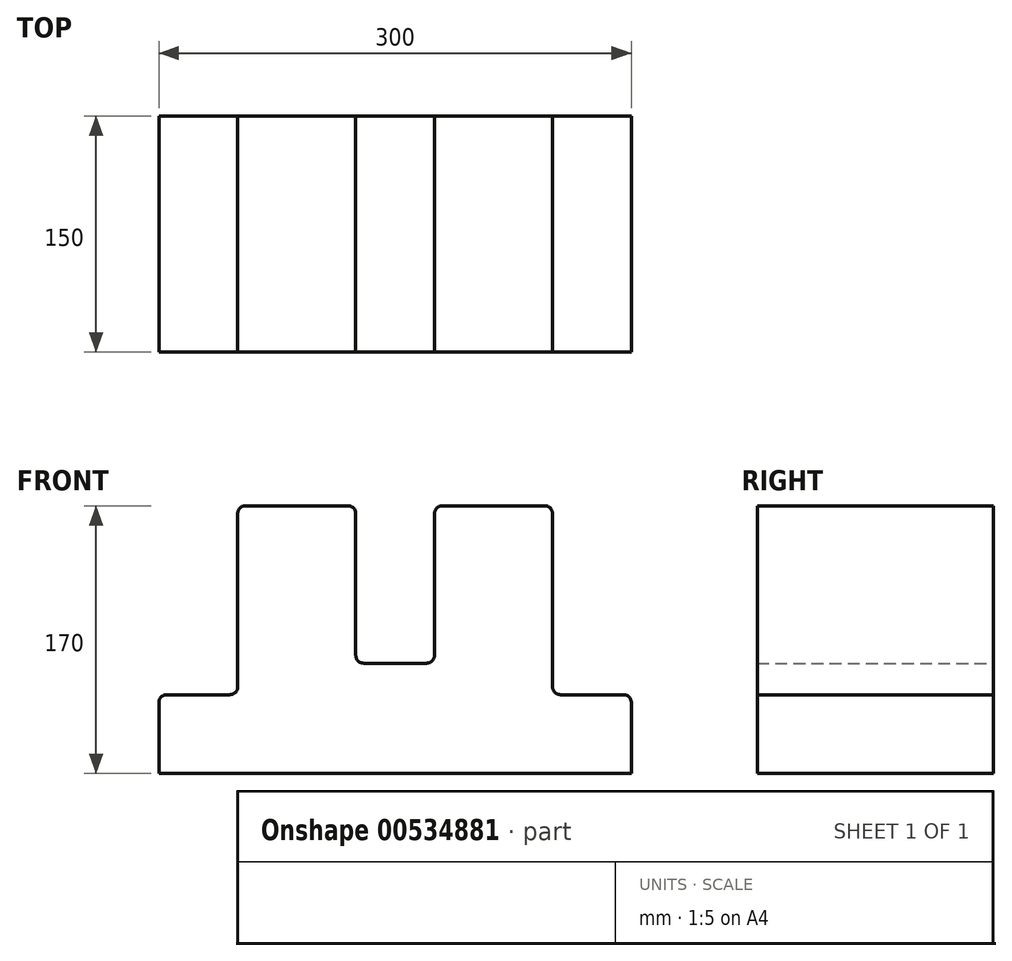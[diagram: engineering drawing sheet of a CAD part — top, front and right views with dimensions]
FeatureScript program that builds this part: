
annotation { "Feature Type Name" : "Feature", "Feature Type Description" : "" }
export const myFeature = defineFeature(function(context is Context, id is Id, definition is map)
    precondition{}
    {
        {
            var Q0;
            Q0=qCreatedBy(makeId("Front.planeOp"),FACE);
            var sketch = newSketch(context, id + "F0", { "sketchPlane" : qUnion([Q0])});
            skLineSegment(sketch, "E0.bottom", {"start": v(-121.73, -43.77) * mm, "end": v(178.27, -43.77) * mm});
            skLineSegment(sketch, "E0.top", {"start": v(-121.73, -93.77) * mm, "end": v(178.27, -93.77) * mm});
            skLineSegment(sketch, "E0.left", {"start": v(-121.73, -43.77) * mm, "end": v(-121.73, -93.77) * mm});
            skLineSegment(sketch, "E0.right", {"start": v(178.27, -43.77) * mm, "end": v(178.27, -93.77) * mm});
            skLineSegment(sketch, "E1.bottom", {"start": v(-71.73, 76.23) * mm, "end": v(3.27, 76.23) * mm});
            skLineSegment(sketch, "E1.top", {"start": v(-71.73, -43.77) * mm, "end": v(128.27, -43.77) * mm});
            skLineSegment(sketch, "E1.left", {"start": v(-71.73, 76.23) * mm, "end": v(-71.73, -43.77) * mm});
            skLineSegment(sketch, "E1.right", {"start": v(128.27, 76.23) * mm, "end": v(128.27, -43.77) * mm});
            skLineSegment(sketch, "E2.top", {"start": v(3.27, -23.77) * mm, "end": v(53.27, -23.77) * mm});
            skLineSegment(sketch, "E2.left", {"start": v(3.27, 76.23) * mm, "end": v(3.27, -23.77) * mm});
            skLineSegment(sketch, "E2.right", {"start": v(53.27, 76.23) * mm, "end": v(53.27, -23.77) * mm});
            skLineSegment(sketch, "E3.trimOffspring", {"start": v(53.27, 76.23) * mm, "end": v(128.27, 76.23) * mm});
            skSolve(sketch);
        }
        {
            var Q0;
            Q0 = qSketchRegion(id + "F0", true);
            extrude(context, id + "F1", {"entities" : qUnion([Q0]), "endBound" : BoundingType.SYMMETRIC, "depth" : 150 * mm, "offsetDistance" : 25 * mm});
        }
        {
            var Q0;
            Q0=makeQuery(id+"F1.opExtrude","SWEPT_EDGE",EDGE,{"disambiguationData":[OSD([sQuery(id+"F0.wireOp",EDGE,"E2.right"),sQuery(id+"F0.wireOp",EDGE,"E3.trimOffspring")])]});
            var Q1;
            Q1=makeQuery(id+"F1.opExtrude","SWEPT_EDGE",EDGE,{"disambiguationData":[OSD([sQuery(id+"F0.wireOp",EDGE,"E1.bottom"),sQuery(id+"F0.wireOp",EDGE,"E2.left")])]});
            var Q2;
            Q2=makeQuery(id+"F1.opExtrude","SWEPT_EDGE",EDGE,{"disambiguationData":[OSD([sQuery(id+"F0.wireOp",EDGE,"E1.right"),sQuery(id+"F0.wireOp",EDGE,"E3.trimOffspring")])]});
            var Q3;
            Q3=makeQuery(id+"F1.opExtrude","SWEPT_EDGE",EDGE,{"disambiguationData":[OSD([sQuery(id+"F0.wireOp",EDGE,"E1.bottom"),sQuery(id+"F0.wireOp",EDGE,"E1.left")])]});
            var Q4;
            Q4=makeQuery(id+"F1.opExtrude","SWEPT_EDGE",EDGE,{"disambiguationData":[OSD([sQuery(id+"F0.wireOp",EDGE,"E0.bottom"),sQuery(id+"F0.wireOp",EDGE,"E1.top"),sQuery(id+"F0.wireOp",EDGE,"E1.left")])]});
            var Q5;
            Q5=makeQuery(id+"F1.opExtrude","SWEPT_EDGE",EDGE,{"disambiguationData":[OSD([sQuery(id+"F0.wireOp",EDGE,"E0.bottom"),sQuery(id+"F0.wireOp",EDGE,"E0.left")])]});
            var Q6;
            Q6=makeQuery(id+"F1.opExtrude","SWEPT_EDGE",EDGE,{"disambiguationData":[OSD([sQuery(id+"F0.wireOp",EDGE,"E0.bottom"),sQuery(id+"F0.wireOp",EDGE,"E1.top"),sQuery(id+"F0.wireOp",EDGE,"E1.right")])]});
            var Q7;
            Q7=makeQuery(id+"F1.opExtrude","SWEPT_EDGE",EDGE,{"disambiguationData":[OSD([sQuery(id+"F0.wireOp",EDGE,"E0.bottom"),sQuery(id+"F0.wireOp",EDGE,"E0.right")])]});
            var Q8;
            Q8=makeQuery(id+"F1.opExtrude","SWEPT_EDGE",EDGE,{"disambiguationData":[OSD([sQuery(id+"F0.wireOp",EDGE,"E2.top"),sQuery(id+"F0.wireOp",EDGE,"E2.left")])]});
            var Q9;
            Q9=makeQuery(id+"F1.opExtrude","SWEPT_EDGE",EDGE,{"disambiguationData":[OSD([sQuery(id+"F0.wireOp",EDGE,"E2.top"),sQuery(id+"F0.wireOp",EDGE,"E2.right")])]});
            fillet(context, id + "F2", {"entities" : qUnion([Q0, Q1, Q2, Q3, Q4, Q5, Q6, Q7, Q8, Q9]), "radius" : 5 * mm, "tangentPropagation" : true, "allowEdgeOverflow" : false});
        }
    });
